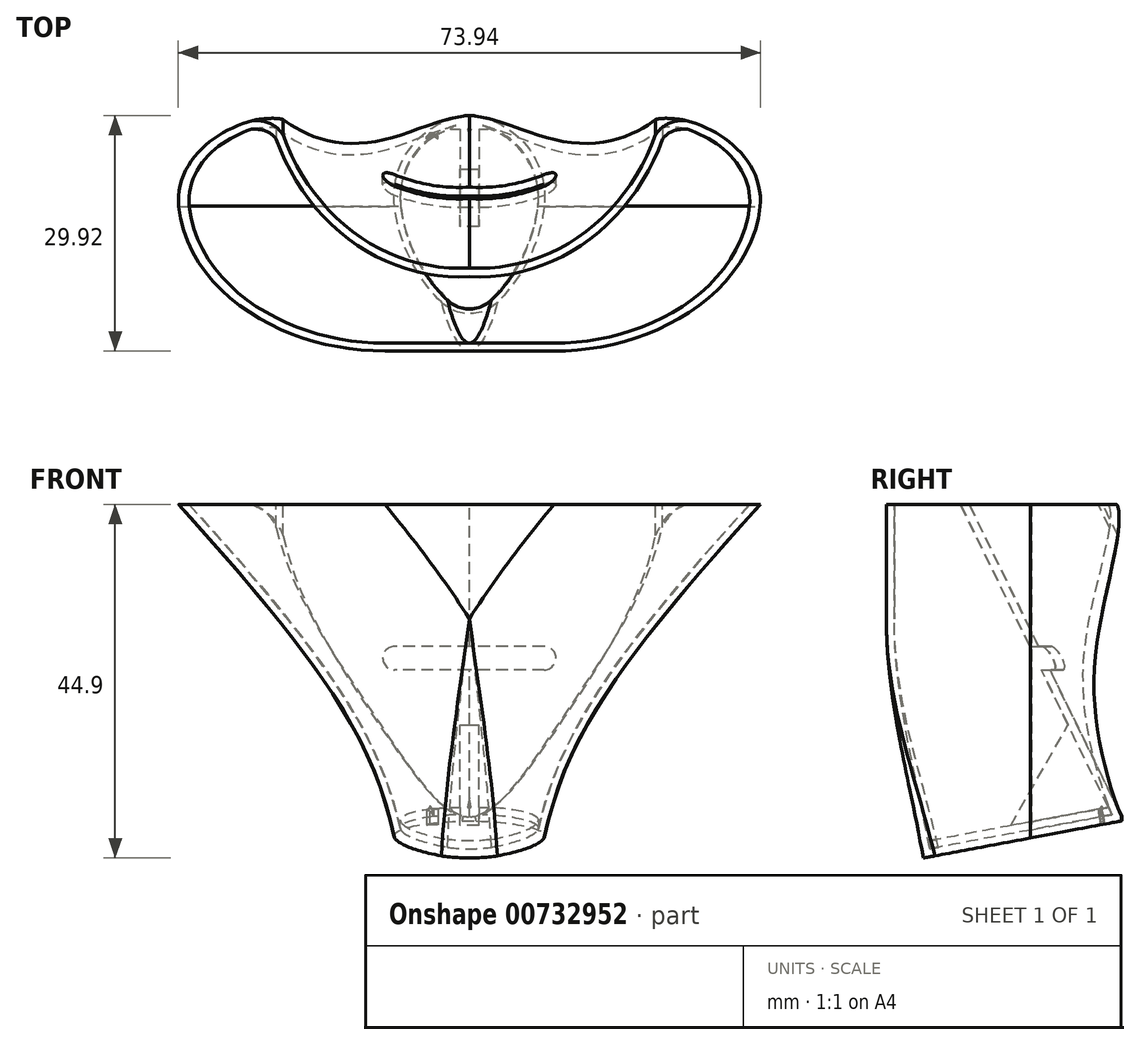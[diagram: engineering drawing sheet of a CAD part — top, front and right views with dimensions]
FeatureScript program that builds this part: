
annotation { "Feature Type Name" : "Feature", "Feature Type Description" : "" }
export const myFeature = defineFeature(function(context is Context, id is Id, definition is map)
    precondition{}
    {
        {
            var Q0;
            Q0=qCreatedBy(makeId("Front.planeOp"),FACE);
            var sketch = newSketch(context, id + "F0", { "sketchPlane" : qUnion([Q0])});
            skLineSegment(sketch, "E0", {"start": v(-9, -21.86) * mm, "end": v(9, -21.86) * mm});
            skLineSegment(sketch, "E1", {"start": v(0, -21.86) * mm, "end": v(0, 23.14) * mm, "construction": true});
            skLineSegment(sketch, "E2", {"start": v(-37, 23.14) * mm, "end": v(37, 23.14) * mm});
            skFitSpline(sketch, "E3", {"points": [v(-37, 23.14) * mm, v(-9, -21.86) * mm], "startDerivative": vector(66.87, -73.39) * mm, "endDerivative": vector(7.33, -37.29) * mm});
            skFitSpline(sketch, "E4.MirrorCS", {"points": [v(37, 23.14) * mm, v(9, -21.86) * mm], "startDerivative": vector(-66.87, -73.39) * mm, "endDerivative": vector(-7.33, -37.29) * mm});
            skSolve(sketch);
        }
        {
            var Q0;
            Q0=makeQuery(id+"F0.imprint","IMPRINT",FACE,{"disambiguationData":[TD([[makeQuery(id+"F0.imprint","IMPRINT",EDGE,{"derivedFrom":sQuery(id+"F0.wireOp",EDGE,"E0")}),1.0]])]});
            extrude(context, id + "F1", {"entities" : qUnion([Q0]), "depth" : 30 * mm, "offsetDistance" : 25 * mm});
        }
        {
            var Q0;
            Q0=makeQuery(id+"F1.opExtrude","CAP_EDGE",EDGE,{"disambiguationData":[OSD([sQuery(id+"F0.wireOp",EDGE,"E3")])],"isStart":false});
            var Q1;
            Q1=makeQuery(id+"F1.opExtrude","CAP_EDGE",EDGE,{"disambiguationData":[OSD([sQuery(id+"F0.wireOp",EDGE,"E4.MirrorCS")])],"isStart":false});
            fillet(context, id + "F2", {"entities" : qUnion([Q0, Q1]), "radius" : 19.8 * mm, "tangentPropagation" : true, "allowEdgeOverflow" : false});
        }
        {
            var Q0;
            Q0=makeQuery(id+"F1.opExtrude","CAP_EDGE",EDGE,{"disambiguationData":[OSD([sQuery(id+"F0.wireOp",EDGE,"E3")])],"isStart":true});
            var Q1;
            Q1=makeQuery(id+"F1.opExtrude","CAP_EDGE",EDGE,{"disambiguationData":[OSD([sQuery(id+"F0.wireOp",EDGE,"E4.MirrorCS")])],"isStart":true});
            fillet(context, id + "F3", {"entities" : qUnion([Q0, Q1]), "radius" : 10.86 * mm, "tangentPropagation" : true, "allowEdgeOverflow" : false});
        }
        {
            var Q0;
            Q0=makeQuery(id+"F2.opFillet","BLEND_EDGE",EDGE,{"blendedFrom":[makeQuery(id+"F1.opExtrude","CAP_EDGE",EDGE,{"disambiguationData":[OSD([sQuery(id+"F0.wireOp",EDGE,"E3")])],"isStart":false}),makeQuery(id+"F1.opExtrude","CAP_EDGE",EDGE,{"disambiguationData":[OSD([sQuery(id+"F0.wireOp",EDGE,"E4.MirrorCS")])],"isStart":false})],"blendedInto":[]});
            fillet(context, id + "F4", {"entities" : qUnion([Q0]), "radius" : 5 * mm, "tangentPropagation" : true, "allowEdgeOverflow" : false});
        }
        {
            var Q0;
            Q0=makeQuery(id+"F3.opFillet","BLEND_EDGE",EDGE,{"blendedFrom":[makeQuery(id+"F1.opExtrude","CAP_EDGE",EDGE,{"disambiguationData":[OSD([sQuery(id+"F0.wireOp",EDGE,"E3")])],"isStart":true}),makeQuery(id+"F1.opExtrude","CAP_EDGE",EDGE,{"disambiguationData":[OSD([sQuery(id+"F0.wireOp",EDGE,"E4.MirrorCS")])],"isStart":true})],"blendedInto":[]});
            fillet(context, id + "F5", {"entities" : qUnion([Q0]), "radius" : 5 * mm, "tangentPropagation" : true, "allowEdgeOverflow" : false});
        }
        {
            var Q0;
            Q0=qCreatedBy(makeId("Right.planeOp"),FACE);
            var sketch = newSketch(context, id + "F6", { "sketchPlane" : qUnion([Q0])});
            skLineSegment(sketch, "E5", {"start": v(-31.86, -23) * mm, "end": v(8.16, -15.5) * mm});
            skLineSegment(sketch, "E6", {"start": v(8.16, -15.5) * mm, "end": v(3.01, -25.08) * mm});
            skLineSegment(sketch, "E7", {"start": v(3.01, -25.08) * mm, "end": v(-31.86, -23) * mm});
            skSolve(sketch);
        }
        {
            var Q0;
            Q0=qSketchRegion(id+"F6",true);
            extrude(context, id + "F7", {"entities" : qUnion([Q0]), "operationType" : NewBodyOperationType.REMOVE, "depth" : 25 * mm, "offsetDistance" : 25 * mm, "hasSecondDirection" : true, "secondDirectionOppositeDirection" : true, "secondDirectionDepth" : 25 * mm});
        }
        {
            var Q0;
            Q0=qCreatedBy(makeId("Right.planeOp"),FACE);
            var sketch = newSketch(context, id + "F8", { "sketchPlane" : qUnion([Q0])});
            skLineSegment(sketch, "E8", {"start": v(-24.08, 32.66) * mm, "end": v(0, 44.42) * mm});
            skSolve(sketch);
        }
        {
            var Q0;
            Q0=sQuery(id+"F8.wireOp",EDGE,"E8");
            extrude(context, id + "F9", {"bodyType" : ToolBodyType.SURFACE, "surfaceEntities" : qUnion([Q0]), "depth" : 25 * mm, "offsetDistance" : 25 * mm, "hasSecondDirection" : true, "secondDirectionOppositeDirection" : true, "secondDirectionDepth" : 25 * mm});
        }
        {
            var Q0;
            Q0=makeQuery(id+"F9.opExtrude","SWEPT_FACE",FACE,{"disambiguationData":[OSD([sQuery(id+"F8.wireOp",EDGE,"E8")])]});
            var sketch = newSketch(context, id + "F10", { "sketchPlane" : qUnion([Q0])});
            skArc(sketch, "E9", {"start": v(23.67, -7.9) * mm, "mid": v(14.28, 3.52) * mm, "end": v(0, 7.3) * mm});
            skFitSpline(sketch, "E10", {"points": [v(23.67, -7.9) * mm, v(31.63, -8.58) * mm], "startDerivative": vector(3.77, -5) * mm, "endDerivative": vector(13, 4.88) * mm});
            skLineSegment(sketch, "E11", {"start": v(31.63, -8.58) * mm, "end": v(10.84, -28.18) * mm});
            skLineSegment(sketch, "E12", {"start": v(10.84, -28.18) * mm, "end": v(0, -18.9) * mm});
            skLineSegment(sketch, "E13", {"start": v(0, 4.27) * mm, "end": v(0, -45.58) * mm, "construction": true});
            skFitSpline(sketch, "E14.MirrorCS", {"points": [v(-23.67, -7.9) * mm, v(-31.63, -8.58) * mm], "startDerivative": vector(-3.77, -5) * mm, "endDerivative": vector(-13, 4.88) * mm});
            skLineSegment(sketch, "E15.MirrorCS", {"start": v(-31.63, -8.58) * mm, "end": v(-10.84, -28.18) * mm});
            skLineSegment(sketch, "E16.MirrorCS", {"start": v(-10.84, -28.18) * mm, "end": v(0, -18.9) * mm});
            skArc(sketch, "E17.MirrorCS", {"start": v(-23.67, -7.9) * mm, "mid": v(-14.28, 3.52) * mm, "end": v(0, 7.3) * mm});
            skPoint(sketch, "E18.orphan", {"position": v(-24.25, -9.56) * mm});
            skPoint(sketch, "E19.orphan", {"position": v(24.25, -9.56) * mm});
            skSolve(sketch);
        }
        {
            var Q0;
            Q0 = qSketchRegion(id + "F10", true);
            extrude(context, id + "F11", {"entities" : qUnion([Q0]), "operationType" : NewBodyOperationType.REMOVE, "depth" : 77.2 * mm, "offsetDistance" : 25 * mm});
        }
        {
            var Q0;
            Q0=makeQuery(id+"F9.opExtrude","SWEPT_BODY",BODY,{"disambiguationData":[OSD([sQuery(id+"F8.wireOp",EDGE,"E8")])]});
            deleteBodies(context, id + "F12", {"entities" : qUnion([Q0])});
        }
        {
            var Q0;
            Q0=makeQuery(id+"F1.opExtrude","SWEPT_FACE",FACE,{"disambiguationData":[OSD([sQuery(id+"F0.wireOp",EDGE,"E2")])]});
            shell(context, id + "F13", {"entities" : qUnion([Q0]), "thickness" : 1 * mm});
        }
        {
            var Q0;
            Q0=makeQuery(id+"F7.boolean.opBoolean","COPY",FACE,{"derivedFrom":makeQuery(id+"F7.opExtrude","SWEPT_FACE",FACE,{"disambiguationData":[OSD([sQuery(id+"F6.wireOp",EDGE,"E5")])]})});
            var sketch = newSketch(context, id + "F14", { "sketchPlane" : qUnion([Q0])});
            skFitSpline(sketch, "E20", {"points": [v(-5.51, 5.37) * mm, v(-4, 5.85) * mm, v(-3.4, 8.02) * mm, v(-5.7, 12.02) * mm, v(-4.58, 21.11) * mm, v(0, 25.37) * mm], "startDerivative": vector(11.33, -0.98) * mm, "endDerivative": vector(15.89, -0.05) * mm});
            skFitSpline(sketch, "E21.MirrorCS", {"points": [v(5.51, 5.37) * mm, v(4, 5.85) * mm, v(3.4, 8.02) * mm, v(5.7, 12.02) * mm, v(4.58, 21.11) * mm, v(0, 25.37) * mm], "startDerivative": vector(-11.33, -0.98) * mm, "endDerivative": vector(-15.89, -0.05) * mm});
            skFitSpline(sketch, "E22", {"points": [v(0, 27.88) * mm, v(-2.51, 27.15) * mm, v(-6.1, 22.7) * mm, v(-7.89, 18.78) * mm, v(-8.68, 15.18) * mm, v(-8.46, 11.07) * mm, v(-6.69, 7.46) * mm, v(-4.98, 5.4) * mm], "startDerivative": vector(-23.61, -0.54) * mm, "endDerivative": vector(20.39, -26.15) * mm});
            skArc(sketch, "E23.filletArc", {"start": v(-5.43, 5.96) * mm, "mid": v(-4.73, 5.6) * mm, "end": v(-3.99, 5.85) * mm});
            skFitSpline(sketch, "E24.MirrorCS", {"points": [v(0, 27.88) * mm, v(2.51, 27.15) * mm, v(6.1, 22.7) * mm, v(7.89, 18.78) * mm, v(8.68, 15.18) * mm, v(8.46, 11.07) * mm, v(6.69, 7.46) * mm, v(4.98, 5.4) * mm], "startDerivative": vector(23.61, -0.54) * mm, "endDerivative": vector(-20.39, -26.15) * mm});
            skArc(sketch, "E25.MirrorCS", {"start": v(5.43, 5.96) * mm, "mid": v(4.73, 5.6) * mm, "end": v(3.99, 5.85) * mm});
            skSolve(sketch);
        }
        {
            var Q0;
            Q0=makeQuery(id+"F14.imprint","IMPRINT",FACE,{"disambiguationData":[TD([[makeQuery(id+"F14.imprint","IMPRINT",EDGE,{"derivedFrom":sQuery(id+"F14.wireOp",EDGE,"E20")}),1.0]])]});
            extrude(context, id + "F15", {"entities" : qUnion([Q0]), "operationType" : NewBodyOperationType.REMOVE, "oppositeDirection" : true, "depth" : 3 * mm, "offsetDistance" : 25 * mm});
        }
        {
            var Q0;
            Q0=qCreatedBy(makeId("Right.planeOp"),FACE);
            var sketch = newSketch(context, id + "F16", { "sketchPlane" : qUnion([Q0])});
            skLineSegment(sketch, "E26", {"start": v(-14.52, -18.2) * mm, "end": v(-6.85, -4.74) * mm});
            skLineSegment(sketch, "E27", {"start": v(-6.85, -4.74) * mm, "end": v(-1.66, -15.56) * mm});
            skLineSegment(sketch, "E28", {"start": v(-1.66, -15.56) * mm, "end": v(-14.52, -18.2) * mm});
            skSolve(sketch);
        }
        {
            var Q0;
            Q0 = qSketchRegion(id + "F16", true);
            extrude(context, id + "F17", {"entities" : qUnion([Q0]), "operationType" : NewBodyOperationType.ADD, "depth" : 1.2 * mm, "offsetDistance" : 25 * mm, "hasSecondDirection" : true, "secondDirectionOppositeDirection" : true, "secondDirectionDepth" : 1.2 * mm});
        }
        {
            var Q0;
            Q0=makeQuery(id+"F14.imprint","IMPRINT",FACE,{"disambiguationData":[TD([[makeQuery(id+"F14.imprint","IMPRINT",EDGE,{"derivedFrom":sQuery(id+"F14.wireOp",EDGE,"E20")}),1.0]])]});
            extrude(context, id + "F18", {"entities" : qUnion([Q0]), "operationType" : NewBodyOperationType.REMOVE, "oppositeDirection" : true, "depth" : 3 * mm, "offsetDistance" : 25 * mm});
        }
        {
            var Q0;
            Q0=qCreatedBy(makeId("Front.planeOp"),FACE);
            var sketch = newSketch(context, id + "F19", { "sketchPlane" : qUnion([Q0])});
            skLineSegment(sketch, "E29.bottom", {"start": v(9.5, 2.13) * mm, "end": v(-9.5, 2.13) * mm});
            skLineSegment(sketch, "E29.top", {"start": v(9.5, 5.13) * mm, "end": v(-9.5, 5.13) * mm});
            skLineSegment(sketch, "E29.left", {"start": v(11, 3.63) * mm, "end": v(11, 3.63) * mm});
            skLineSegment(sketch, "E29.right", {"start": v(-11, 3.63) * mm, "end": v(-11, 3.63) * mm});
            skPoint(sketch, "E29.middle", {"position": v(0, 3.63) * mm});
            skPoint(sketch, "E30.visualSharp", {"position": v(11, 5.13) * mm});
            skArc(sketch, "E30.filletArc", {"start": v(11, 3.63) * mm, "mid": v(10.56, 4.7) * mm, "end": v(9.5, 5.13) * mm});
            skPoint(sketch, "E31.visualSharp", {"position": v(11, 2.13) * mm});
            skArc(sketch, "E31.filletArc", {"start": v(9.5, 2.13) * mm, "mid": v(10.56, 2.57) * mm, "end": v(11, 3.63) * mm});
            skPoint(sketch, "E32.visualSharp", {"position": v(-11, 5.13) * mm});
            skArc(sketch, "E32.filletArc", {"start": v(-9.5, 5.13) * mm, "mid": v(-10.56, 4.7) * mm, "end": v(-11, 3.63) * mm});
            skPoint(sketch, "E33.visualSharp", {"position": v(-11, 2.13) * mm});
            skArc(sketch, "E33.filletArc", {"start": v(-11, 3.63) * mm, "mid": v(-10.56, 2.57) * mm, "end": v(-9.5, 2.13) * mm});
            skSolve(sketch);
        }
        {
            var Q0;
            Q0 = qSketchRegion(id + "F19", true);
            extrude(context, id + "F20", {"entities" : qUnion([Q0]), "operationType" : NewBodyOperationType.REMOVE, "depth" : 13.5 * mm, "offsetDistance" : 25 * mm});
        }
        {
            var Q0;
            Q0=makeQuery(id+"F15.boolean.opBoolean","SPLIT",FACE,{"disambiguationData":[TD([makeQuery(id+"F13.opShell","OFFSET_FACE",FACE,{"disambiguationData":[OSD([sQuery(id+"F10.wireOp",EDGE,"E9")])]})])],"derivedFrom":makeQuery(id+"F13.opShell","OFFSET_FACE",FACE,{"disambiguationData":[OSD([sQuery(id+"F6.wireOp",EDGE,"E5")])]})});
            extrude(context, id + "F21", {"entities" : qUnion([Q0]), "operationType" : NewBodyOperationType.ADD, "depth" : 1 * mm, "offsetDistance" : 25 * mm});
        }
    });
